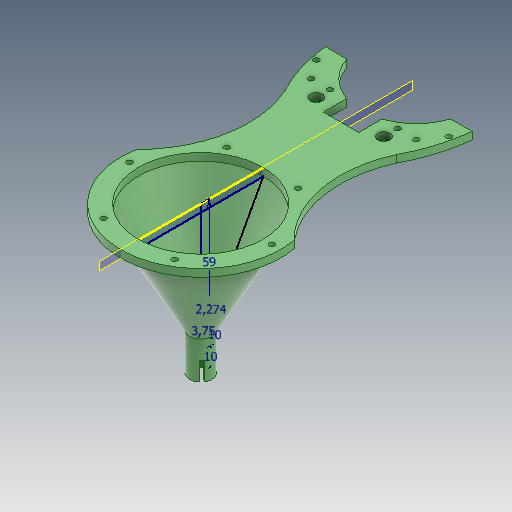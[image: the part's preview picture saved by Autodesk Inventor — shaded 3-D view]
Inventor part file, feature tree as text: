
AUTODESK INVENTOR PART (.ipt)
format: ipt  version: 2020.3 (Build 243373000, 373)  size: 284,160 bytes
history: native  units: mm
features: sketch x2, revolve x2, extrude x1, plane x1, pattern_circular x1
ambient origin geometry x8: Origin, YZ Plane, XZ Plane, XY Plane, X Axis, Y Axis, Z Axis, Center Point
bodies: Solid1 (feature_tree)
feature tree (7):
  extrude  "Extrusion1"  Depth=60.0mm TaperAngle=90.0deg
  plane  "Work Plane1"
  sketch  "Sketch3"  dims[d42=12.833071mm d43=12.833071mm d44=2.0mm d45=6.5mm d46=2.0mm d47=2.0mm d48=67.0mm d49=30.0mm d52=42.0mm d57=3.0mm d58=60.0mm d60=360.0deg d62=4.0mm d63=0.0mm d84=4.75mm d85=60.0mm d86=25.0mm d88=59.0mm d89=3.75mm d94=10.0mm d96=2.273836mm d97=90.0deg d98=10.0mm d99=17.453293mm d100=30.0mm d101=360.0deg]
  revolve  "Revolution4"  [1 undecoded]
  revolve  "Revolution5"  [1 undecoded]
  pattern_circular  "Circular Pattern3"  [2 undecoded]
  sketch  "Sketch1"  dims[d1=40.0mm d3=20.0mm d5=200.0mm d6=60.0mm d7=81.0mm d8=3.0mm d9=7.5mm d10=5.0mm d11=30.0mm d12=3.0mm d13=7.5mm d14=5.0mm d15=3.0mm d16=3.0mm d17=5.0mm d18=48.0mm d19=55.0mm d20=3.0mm d21=4.5mm d22=3.0mm d23=4.5mm d24=360.0deg d25=80.0mm d26=72.56mm d27=3.0mm d28=3.0mm d29=360.0deg d30=45.0deg d31=3.0mm d32=360.0deg d33=3.0mm d34=3.0mm d35=3.0mm d36=3.0mm d37=55.0mm d38=80.0mm d39=90.0deg]
note: 4 required parameter values undecoded (feature->parameter linkage not recoverable at this tier; creation-order binding heuristic only, values carry confidence <= 0.55)